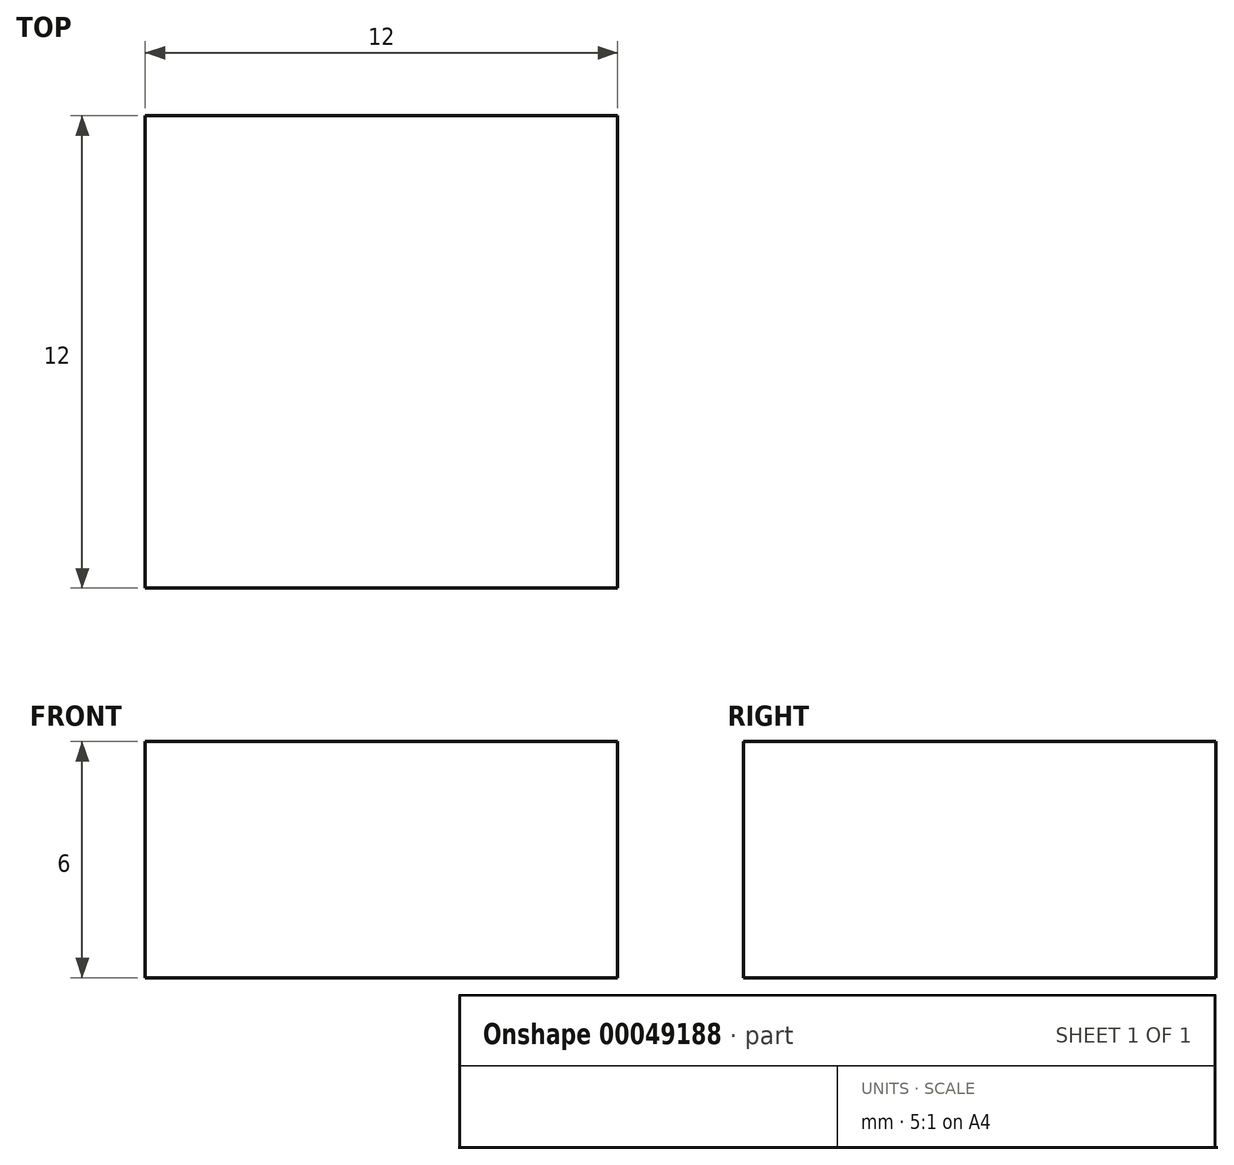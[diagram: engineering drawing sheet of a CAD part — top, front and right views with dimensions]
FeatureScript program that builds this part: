
annotation { "Feature Type Name" : "Feature", "Feature Type Description" : "" }
export const myFeature = defineFeature(function(context is Context, id is Id, definition is map)
    precondition{}
    {
        {
            var Q0;
            Q0=qCreatedBy(makeId("Top.planeOp"),FACE);
            var sketch = newSketch(context, id + "F0", { "sketchPlane" : qUnion([Q0])});
            skLineSegment(sketch, "E0.rect.bottom", {"start": v(6, 6) * mm, "end": v(-6, 6) * mm});
            skLineSegment(sketch, "E0.rect.top", {"start": v(6, -6) * mm, "end": v(-6, -6) * mm});
            skLineSegment(sketch, "E0.rect.left", {"start": v(6, 6) * mm, "end": v(6, -6) * mm});
            skLineSegment(sketch, "E0.rect.right", {"start": v(-6, 6) * mm, "end": v(-6, -6) * mm});
            skPoint(sketch, "E0.rect.middle", {"position": v(0, 0) * mm});
            skSolve(sketch);
        }
        {
            var Q0;
            Q0=makeQuery(id+"F0.imprint","IMPRINT",FACE,{"disambiguationData":[TD([[makeQuery(id+"F0.imprint","IMPRINT",EDGE,{"derivedFrom":sQuery(id+"F0.wireOp",EDGE,"E0.rect.bottom")}),1.0]])]});
            extrude(context, id + "F1", {"entities" : qUnion([Q0]), "depth" : 6 * mm});
        }
        {
            var Q0;
            Q0=makeQuery(id+"F1.opExtrude","CAP_FACE",FACE,{"disambiguationData":[OSD([sQuery(id+"F0.wireOp",EDGE,"E0.rect.bottom"),sQuery(id+"F0.wireOp",EDGE,"E0.rect.top"),sQuery(id+"F0.wireOp",EDGE,"E0.rect.left"),sQuery(id+"F0.wireOp",EDGE,"E0.rect.right")])],"isStart":false});
            var sketch = newSketch(context, id + "F2", { "sketchPlane" : qUnion([Q0])});
            skCircle(sketch, "E1", {"center": v(0, 0) * mm, "radius": 3.1 * mm});
            skSolve(sketch);
        }
        {
            var Q0;
            Q0=sQuery(id+"F2.wireOp",EDGE,"E1");
            extrude(context, id + "F3", {"bodyType" : ToolBodyType.SURFACE, "surfaceEntities" : qUnion([Q0]), "oppositeDirection" : true, "depth" : 4 * mm});
        }
    });
